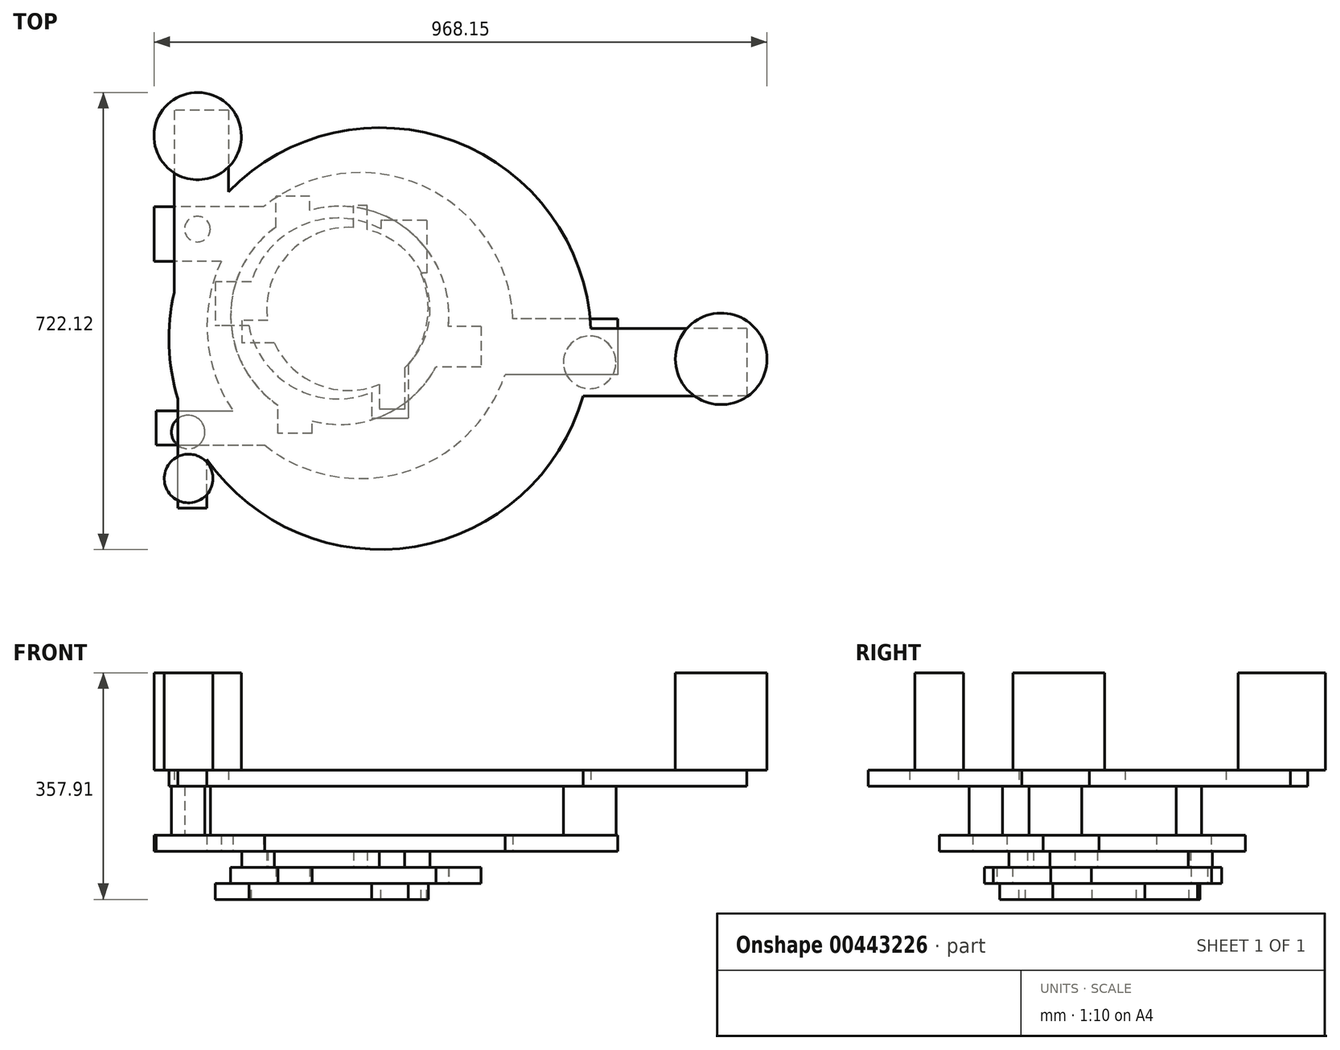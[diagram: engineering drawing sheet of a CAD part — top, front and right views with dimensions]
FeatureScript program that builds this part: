
annotation { "Feature Type Name" : "Feature", "Feature Type Description" : "" }
export const myFeature = defineFeature(function(context is Context, id is Id, definition is map)
    precondition{}
    {
        {
            var Q0;
            Q0=qCreatedBy(makeId("Top.planeOp"),FACE);
            var sketch = newSketch(context, id + "F0", { "sketchPlane" : qUnion([Q0])});
            skCircle(sketch, "E0", {"center": v(-32.41, 49.4) * mm, "radius": 172.38 * mm});
            skPoint(sketch, "E0.first.point", {"position": v(-103.26, -107.75) * mm});
            skPoint(sketch, "E0.second.point", {"position": v(-106.6, 205) * mm});
            skPoint(sketch, "E0.third.point", {"position": v(132.73, 0) * mm});
            skLineSegment(sketch, "E1.bottom", {"start": v(190.33, 32.03) * mm, "end": v(75.14, 32.03) * mm});
            skLineSegment(sketch, "E1.top", {"start": v(190.33, -32.03) * mm, "end": v(75.14, -32.03) * mm});
            skLineSegment(sketch, "E1.left", {"start": v(190.33, 32.03) * mm, "end": v(190.33, -32.03) * mm});
            skLineSegment(sketch, "E1.right", {"start": v(75.14, 32.03) * mm, "end": v(75.14, -32.03) * mm});
            skLineSegment(sketch, "E2.bottom", {"start": v(-79.68, 172.38) * mm, "end": v(-133.53, 172.38) * mm});
            skLineSegment(sketch, "E2.top", {"start": v(-79.68, 237.62) * mm, "end": v(-133.53, 237.62) * mm});
            skLineSegment(sketch, "E2.left", {"start": v(-79.68, 172.38) * mm, "end": v(-79.68, 237.62) * mm});
            skLineSegment(sketch, "E2.right", {"start": v(-133.53, 172.38) * mm, "end": v(-133.53, 237.62) * mm});
            skLineSegment(sketch, "E3.bottom", {"start": v(-76.26, -137.06) * mm, "end": v(-130.26, -137.06) * mm});
            skLineSegment(sketch, "E3.top", {"start": v(-76.26, -78.44) * mm, "end": v(-130.26, -78.44) * mm});
            skLineSegment(sketch, "E3.left", {"start": v(-76.26, -137.06) * mm, "end": v(-76.26, -78.44) * mm});
            skLineSegment(sketch, "E3.right", {"start": v(-130.26, -137.06) * mm, "end": v(-130.26, -78.44) * mm});
            skSolve(sketch);
        }
        {
            var Q0;
            Q0 = qSketchRegion(id + "F0", true);
            extrude(context, id + "F1", {"entities" : qUnion([Q0]), "depth" : 25.4 * mm});
        }
        {
            var Q0;
            Q0=qCreatedBy(makeId("Top.planeOp"),FACE);
            var sketch = newSketch(context, id + "F2", { "sketchPlane" : qUnion([Q0])});
            skCircle(sketch, "E4", {"center": v(-35.78, 60.24) * mm, "radius": 142.9 * mm});
            skPoint(sketch, "E4.first.point", {"position": v(-178.48, 67.72) * mm});
            skPoint(sketch, "E4.second.point", {"position": v(46.61, -56.5) * mm});
            skPoint(sketch, "E4.third.point", {"position": v(68.48, 157.95) * mm});
            skLineSegment(sketch, "E5.bottom", {"start": v(104.65, 199.6) * mm, "end": v(32.3, 199.6) * mm});
            skLineSegment(sketch, "E5.top", {"start": v(104.65, 116.3) * mm, "end": v(32.3, 116.3) * mm});
            skLineSegment(sketch, "E5.left", {"start": v(104.65, 199.6) * mm, "end": v(104.65, 116.3) * mm});
            skLineSegment(sketch, "E5.right", {"start": v(32.3, 199.6) * mm, "end": v(32.3, 116.3) * mm});
            skLineSegment(sketch, "E6.bottom", {"start": v(-127.72, 102.61) * mm, "end": v(-229.24, 102.61) * mm});
            skLineSegment(sketch, "E6.top", {"start": v(-127.72, 32.83) * mm, "end": v(-229.24, 32.83) * mm});
            skLineSegment(sketch, "E6.left", {"start": v(-127.72, 102.61) * mm, "end": v(-127.72, 32.83) * mm});
            skLineSegment(sketch, "E6.right", {"start": v(-229.24, 102.61) * mm, "end": v(-229.24, 32.83) * mm});
            skLineSegment(sketch, "E7.bottom", {"start": v(17.61, 0) * mm, "end": v(75.61, 0) * mm});
            skLineSegment(sketch, "E7.top", {"start": v(17.61, -113) * mm, "end": v(75.61, -113) * mm});
            skLineSegment(sketch, "E7.left", {"start": v(17.61, 0) * mm, "end": v(17.61, -113) * mm});
            skLineSegment(sketch, "E7.right", {"start": v(75.61, 0) * mm, "end": v(75.61, -113) * mm});
            skSolve(sketch);
        }
        {
            var Q0;
            Q0 = qSketchRegion(id + "F2", true);
            extrude(context, id + "F3", {"entities" : qUnion([Q0]), "operationType" : NewBodyOperationType.ADD, "oppositeDirection" : true, "depth" : 25.4 * mm});
        }
        {
            var Q0;
            Q0=makeQuery(id+"F1.opExtrude","CAP_FACE",FACE,{"disambiguationData":[OSD([sQuery(id+"F0.wireOp",EDGE,"E0"),sQuery(id+"F0.wireOp",EDGE,"E1.bottom"),sQuery(id+"F0.wireOp",EDGE,"E1.top"),sQuery(id+"F0.wireOp",EDGE,"E1.left"),sQuery(id+"F0.wireOp",EDGE,"E2.top"),sQuery(id+"F0.wireOp",EDGE,"E2.left"),sQuery(id+"F0.wireOp",EDGE,"E2.right"),sQuery(id+"F0.wireOp",EDGE,"E3.bottom"),sQuery(id+"F0.wireOp",EDGE,"E3.left"),sQuery(id+"F0.wireOp",EDGE,"E3.right")])],"isStart":false});
            var sketch = newSketch(context, id + "F4", { "sketchPlane" : qUnion([Q0])});
            skCircle(sketch, "E8", {"center": v(-18.82, 59.57) * mm, "radius": 128.82 * mm});
            skPoint(sketch, "E8.first.point", {"position": v(-142.47, 23.46) * mm});
            skPoint(sketch, "E8.second.point", {"position": v(0, 187) * mm});
            skPoint(sketch, "E8.third.point", {"position": v(50, -49.32) * mm});
            skLineSegment(sketch, "E9.bottom", {"start": v(11, 151.18) * mm, "end": v(-11, 151.18) * mm});
            skLineSegment(sketch, "E9.top", {"start": v(11, 222.84) * mm, "end": v(-11, 222.84) * mm});
            skLineSegment(sketch, "E9.left", {"start": v(11, 151.18) * mm, "end": v(11, 222.84) * mm});
            skLineSegment(sketch, "E9.right", {"start": v(-11, 151.18) * mm, "end": v(-11, 222.84) * mm});
            skLineSegment(sketch, "E10.bottom", {"start": v(70.15, 0) * mm, "end": v(29.86, 0) * mm});
            skLineSegment(sketch, "E10.top", {"start": v(70.15, -98.64) * mm, "end": v(29.86, -98.64) * mm});
            skLineSegment(sketch, "E10.left", {"start": v(70.15, 0) * mm, "end": v(70.15, -98.64) * mm});
            skLineSegment(sketch, "E10.right", {"start": v(29.86, 0) * mm, "end": v(29.86, -98.64) * mm});
            skLineSegment(sketch, "E11.bottom", {"start": v(-97.67, 41.08) * mm, "end": v(-187.28, 41.08) * mm});
            skLineSegment(sketch, "E11.top", {"start": v(-97.67, 5.84) * mm, "end": v(-187.28, 5.84) * mm});
            skLineSegment(sketch, "E11.left", {"start": v(-97.67, 41.08) * mm, "end": v(-97.67, 5.84) * mm});
            skLineSegment(sketch, "E11.right", {"start": v(-187.28, 41.08) * mm, "end": v(-187.28, 5.84) * mm});
            skSolve(sketch);
        }
        {
            var Q0;
            Q0 = qSketchRegion(id + "F4", true);
            extrude(context, id + "F5", {"entities" : qUnion([Q0]), "operationType" : NewBodyOperationType.ADD, "depth" : 25.4 * mm});
        }
        {
            var Q0;
            Q0=makeQuery(id+"F5.opExtrude","CAP_FACE",FACE,{"disambiguationData":[OSD([sQuery(id+"F4.wireOp",EDGE,"E8"),sQuery(id+"F4.wireOp",EDGE,"E9.top"),sQuery(id+"F4.wireOp",EDGE,"E9.left"),sQuery(id+"F4.wireOp",EDGE,"E9.right"),sQuery(id+"F4.wireOp",EDGE,"E10.top"),sQuery(id+"F4.wireOp",EDGE,"E10.left"),sQuery(id+"F4.wireOp",EDGE,"E10.right"),sQuery(id+"F4.wireOp",EDGE,"E11.bottom"),sQuery(id+"F4.wireOp",EDGE,"E11.top"),sQuery(id+"F4.wireOp",EDGE,"E11.right")])],"isStart":false});
            var sketch = newSketch(context, id + "F6", { "sketchPlane" : qUnion([Q0])});
            skCircle(sketch, "E12", {"center": v(-0.5, 33.27) * mm, "radius": 241.76 * mm});
            skPoint(sketch, "E12.first.point", {"position": v(-194.3, 177.82) * mm});
            skPoint(sketch, "E12.second.point", {"position": v(-179.97, -128.72) * mm});
            skPoint(sketch, "E12.third.point", {"position": v(238.95, 0) * mm});
            skLineSegment(sketch, "E13.bottom", {"start": v(406.48, 44.1) * mm, "end": v(71.42, 44.1) * mm});
            skLineSegment(sketch, "E13.top", {"start": v(406.48, -44.1) * mm, "end": v(71.42, -44.1) * mm});
            skLineSegment(sketch, "E13.left", {"start": v(406.48, 44.1) * mm, "end": v(406.48, -44.1) * mm});
            skLineSegment(sketch, "E13.right", {"start": v(71.42, 44.1) * mm, "end": v(71.42, -44.1) * mm});
            skLineSegment(sketch, "E14.bottom", {"start": v(-322.41, -155.77) * mm, "end": v(-37.53, -155.77) * mm});
            skLineSegment(sketch, "E14.top", {"start": v(-322.41, -101.67) * mm, "end": v(-37.53, -101.67) * mm});
            skLineSegment(sketch, "E14.left", {"start": v(-322.41, -155.77) * mm, "end": v(-322.41, -101.67) * mm});
            skLineSegment(sketch, "E14.right", {"start": v(-37.53, -155.77) * mm, "end": v(-37.53, -101.67) * mm});
            skLineSegment(sketch, "E15.bottom", {"start": v(-62.64, 220.85) * mm, "end": v(-325.96, 220.85) * mm});
            skLineSegment(sketch, "E15.top", {"start": v(-62.64, 134.78) * mm, "end": v(-325.96, 134.78) * mm});
            skLineSegment(sketch, "E15.left", {"start": v(-62.64, 220.85) * mm, "end": v(-62.64, 134.78) * mm});
            skLineSegment(sketch, "E15.right", {"start": v(-325.96, 220.85) * mm, "end": v(-325.96, 134.78) * mm});
            skSolve(sketch);
        }
        {
            var Q0;
            Q0 = qSketchRegion(id + "F6", true);
            extrude(context, id + "F7", {"entities" : qUnion([Q0]), "operationType" : NewBodyOperationType.ADD, "depth" : 25.4 * mm});
        }
        {
            var Q0;
            Q0=makeQuery(id+"F7.opExtrude","CAP_FACE",FACE,{"disambiguationData":[OSD([sQuery(id+"F6.wireOp",EDGE,"E12"),sQuery(id+"F6.wireOp",EDGE,"E13.bottom"),sQuery(id+"F6.wireOp",EDGE,"E13.top"),sQuery(id+"F6.wireOp",EDGE,"E13.left"),sQuery(id+"F6.wireOp",EDGE,"E14.bottom"),sQuery(id+"F6.wireOp",EDGE,"E14.top"),sQuery(id+"F6.wireOp",EDGE,"E14.left"),sQuery(id+"F6.wireOp",EDGE,"E15.bottom"),sQuery(id+"F6.wireOp",EDGE,"E15.top"),sQuery(id+"F6.wireOp",EDGE,"E15.right")])],"isStart":false});
            var sketch = newSketch(context, id + "F8", { "sketchPlane" : qUnion([Q0])});
            skCircle(sketch, "E16", {"center": v(-271.97, -134.89) * mm, "radius": 26.44 * mm});
            skCircle(sketch, "E17", {"center": v(-257.32, 185.7) * mm, "radius": 20.22 * mm});
            skCircle(sketch, "E18", {"center": v(362.1, -24.8) * mm, "radius": 41.54 * mm});
            skSolve(sketch);
        }
        {
            var Q0;
            Q0 = qSketchRegion(id + "F8", true);
            extrude(context, id + "F9", {"entities" : qUnion([Q0]), "operationType" : NewBodyOperationType.ADD, "depth" : 76.97 * mm});
        }
        {
            var Q0;
            Q0=makeQuery(id+"F9.opExtrude","CAP_FACE",FACE,{"disambiguationData":[OSD([sQuery(id+"F8.wireOp",EDGE,"E18")])],"isStart":false});
            var sketch = newSketch(context, id + "F10", { "sketchPlane" : qUnion([Q0])});
            skCircle(sketch, "E19", {"center": v(31, 12.74) * mm, "radius": 333.23 * mm});
            skPoint(sketch, "E19.first.point", {"position": v(362.1, -24.8) * mm});
            skPoint(sketch, "E19.second.point", {"position": v(-265.31, -139.71) * mm});
            skPoint(sketch, "E19.third.point", {"position": v(-251.22, 189.93) * mm});
            skLineSegment(sketch, "E20.bottom", {"start": v(610.5, 28.59) * mm, "end": v(113.7, 28.59) * mm});
            skLineSegment(sketch, "E20.top", {"start": v(610.5, -78.18) * mm, "end": v(113.7, -78.18) * mm});
            skLineSegment(sketch, "E20.left", {"start": v(610.5, 28.59) * mm, "end": v(610.5, -78.18) * mm});
            skLineSegment(sketch, "E20.right", {"start": v(113.7, 28.59) * mm, "end": v(113.7, -78.18) * mm});
            skLineSegment(sketch, "E21.bottom", {"start": v(-242.22, -255.07) * mm, "end": v(-288.4, -255.07) * mm});
            skLineSegment(sketch, "E21.top", {"start": v(-242.22, -24.36) * mm, "end": v(-288.4, -24.36) * mm});
            skLineSegment(sketch, "E21.left", {"start": v(-242.22, -255.07) * mm, "end": v(-242.22, -24.36) * mm});
            skLineSegment(sketch, "E21.right", {"start": v(-288.4, -255.07) * mm, "end": v(-288.4, -24.36) * mm});
            skLineSegment(sketch, "E22.bottom", {"start": v(-208.22, 373.3) * mm, "end": v(-294.21, 373.3) * mm});
            skLineSegment(sketch, "E22.top", {"start": v(-208.22, 6.56) * mm, "end": v(-294.21, 6.56) * mm});
            skLineSegment(sketch, "E22.left", {"start": v(-208.22, 373.3) * mm, "end": v(-208.22, 6.56) * mm});
            skLineSegment(sketch, "E22.right", {"start": v(-294.21, 373.3) * mm, "end": v(-294.21, 6.56) * mm});
            skSolve(sketch);
        }
        {
            var Q0;
            Q0 = qSketchRegion(id + "F10", true);
            extrude(context, id + "F11", {"entities" : qUnion([Q0]), "operationType" : NewBodyOperationType.ADD, "depth" : 25.4 * mm});
        }
        {
            var Q0;
            Q0=makeQuery(id+"F11.opExtrude","CAP_FACE",FACE,{"disambiguationData":[OSD([sQuery(id+"F10.wireOp",EDGE,"E19"),sQuery(id+"F10.wireOp",EDGE,"E20.bottom"),sQuery(id+"F10.wireOp",EDGE,"E20.top"),sQuery(id+"F10.wireOp",EDGE,"E20.left"),sQuery(id+"F10.wireOp",EDGE,"E21.bottom"),sQuery(id+"F10.wireOp",EDGE,"E21.left"),sQuery(id+"F10.wireOp",EDGE,"E21.right"),sQuery(id+"F10.wireOp",EDGE,"E22.bottom"),sQuery(id+"F10.wireOp",EDGE,"E22.left"),sQuery(id+"F10.wireOp",EDGE,"E22.right")])],"isStart":false});
            var sketch = newSketch(context, id + "F12", { "sketchPlane" : qUnion([Q0])});
            skCircle(sketch, "E23", {"center": v(-271.31, -208.34) * mm, "radius": 38.48 * mm});
            skCircle(sketch, "E24", {"center": v(-256.99, 332.64) * mm, "radius": 69 * mm});
            skCircle(sketch, "E25", {"center": v(569.82, -19.32) * mm, "radius": 72.35 * mm});
            skSolve(sketch);
        }
        {
            var Q0;
            Q0 = qSketchRegion(id + "F12", true);
            extrude(context, id + "F13", {"entities" : qUnion([Q0]), "operationType" : NewBodyOperationType.ADD, "depth" : 153.94 * mm});
        }
    });
